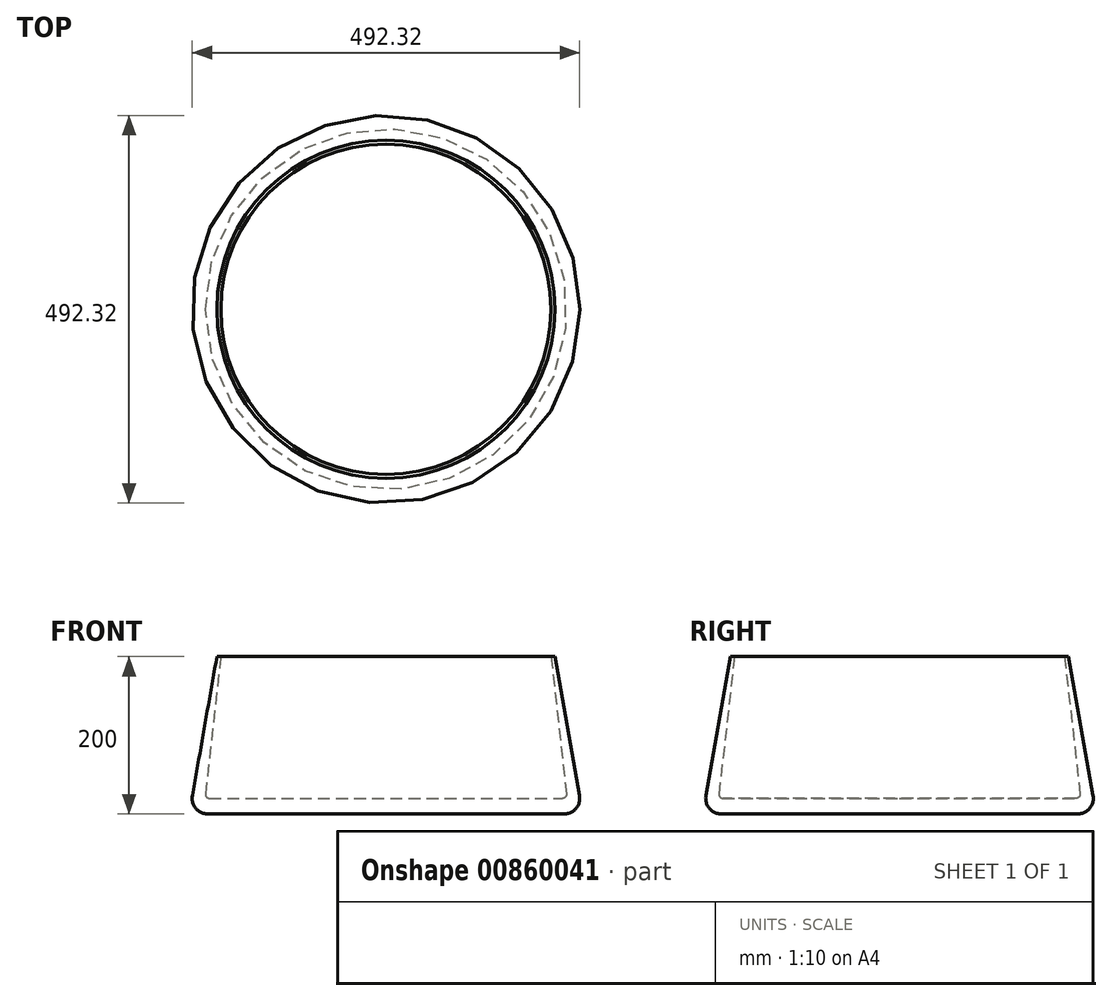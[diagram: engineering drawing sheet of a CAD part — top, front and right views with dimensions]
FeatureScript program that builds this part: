
annotation { "Feature Type Name" : "Feature", "Feature Type Description" : "" }
export const myFeature = defineFeature(function(context is Context, id is Id, definition is map)
    precondition{}
    {
        {
            var Q0;
            Q0=qCreatedBy(makeId("Front.planeOp"),FACE);
            var sketch = newSketch(context, id + "F0", { "sketchPlane" : qUnion([Q0])});
            skLineSegment(sketch, "E0", {"start": v(-214.73, 200) * mm, "end": v(-250, 0) * mm});
            skLineSegment(sketch, "E1", {"start": v(-250, 0) * mm, "end": v(0, 0) * mm});
            skLineSegment(sketch, "E2", {"start": v(0, 0) * mm, "end": v(0, 20) * mm});
            skLineSegment(sketch, "E3", {"start": v(0, 20) * mm, "end": v(-230, 20) * mm});
            skLineSegment(sketch, "E4", {"start": v(-230, 20) * mm, "end": v(-209.73, 200) * mm});
            skLineSegment(sketch, "E5", {"start": v(-209.73, 200) * mm, "end": v(-214.73, 200) * mm});
            skSolve(sketch);
        }
        {
            var Q0;
            Q0=makeQuery(id+"F0.imprint","IMPRINT",FACE,{"disambiguationData":[TD([[makeQuery(id+"F0.imprint","IMPRINT",EDGE,{"derivedFrom":sQuery(id+"F0.wireOp",EDGE,"E0")}),1.0]])]});
            var Q1;
            Q1=sQuery(id+"F0.wireOp",EDGE,"E2");
            revolve(context, id + "F1", {"surfaceOperationType" : NewSurfaceOperationType.NEW, "entities" : qUnion([Q0]), "axis" : qUnion([Q1]), "revolveType" : RevolveType.FULL});
        }
        {
            var Q0;
            Q0=makeQuery(id+"F1.opRevolve","SWEPT_EDGE",EDGE,{"disambiguationData":[OSD([sQuery(id+"F0.wireOp",EDGE,"E0"),sQuery(id+"F0.wireOp",EDGE,"E1")])]});
            fillet(context, id + "F2", {"entities" : qUnion([Q0]), "radius" : 20 * mm, "tangentPropagation" : true, "allowEdgeOverflow" : false});
        }
        {
            var Q0;
            Q0=makeQuery(id+"F1.opRevolve","SWEPT_EDGE",EDGE,{"disambiguationData":[OSD([sQuery(id+"F0.wireOp",EDGE,"E3"),sQuery(id+"F0.wireOp",EDGE,"E4")])]});
            fillet(context, id + "F3", {"entities" : qUnion([Q0]), "radius" : 5 * mm, "tangentPropagation" : true, "allowEdgeOverflow" : false});
        }
    });
